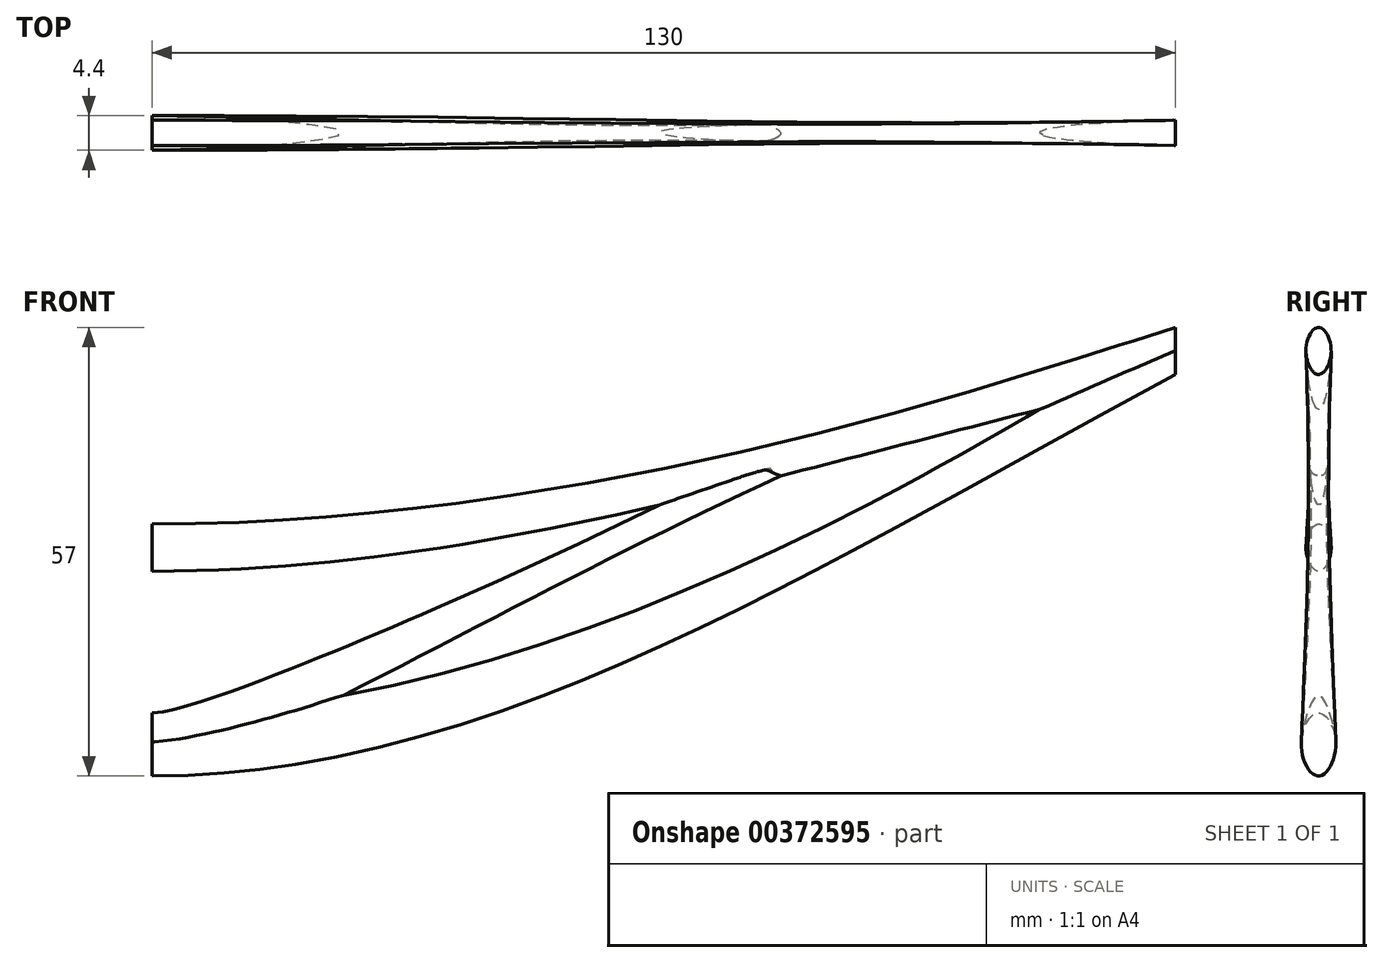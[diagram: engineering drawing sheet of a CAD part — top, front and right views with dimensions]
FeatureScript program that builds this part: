
annotation { "Feature Type Name" : "Feature", "Feature Type Description" : "" }
export const myFeature = defineFeature(function(context is Context, id is Id, definition is map)
    precondition{}
    {
        {
            var Q0;
            Q0=qCreatedBy(makeId("Right.planeOp"),FACE);
            var sketch = newSketch(context, id + "F0", { "sketchPlane" : qUnion([Q0])});
            skFitSpline(sketch, "E0", {"points": [v(-2.2, 0) * mm, v(0, 4) * mm, v(2.2, 0) * mm, v(0, -4) * mm, v(-2.2, 0) * mm]});
            skPoint(sketch, "E1", {"position": v(0, 25) * mm});
            skFitSpline(sketch, "E2", {"points": [v(-1.6, 25) * mm, v(0, 28) * mm, v(1.6, 25) * mm, v(0, 22) * mm, v(-1.6, 25) * mm]});
            skSolve(sketch);
        }
        {
            var Q0;
            Q0=qCreatedBy(makeId("Right.planeOp"),FACE);
            cPlane(context, id + "F1", {"entities" : qUnion([Q0]), "cplaneType" : CPlaneType.OFFSET, "offset" : 130 * mm, "width" : 150 * mm, "height" : 150 * mm});
        }
        {
            var Q0;
            Q0=qCreatedBy(id+"F1.planeOp",FACE);
            var sketch = newSketch(context, id + "F2", { "sketchPlane" : qUnion([Q0])});
            skFitSpline(sketch, "E3", {"points": [v(-1.6, 50) * mm, v(0, 53) * mm, v(1.6, 50) * mm, v(0, 47) * mm, v(-1.6, 50) * mm]});
            skFitSpline(sketch, "E4.0", {"points": [v(-3, 0) * mm, v(-3, 2.5) * mm, v(0, 7.5) * mm, v(4.5, 0) * mm, v(0, -7.5) * mm, v(-3, -2.5) * mm, v(-3, 0) * mm]});
            skPoint(sketch, "E5.0", {"position": v(0, 0) * mm});
            skLineSegment(sketch, "E6", {"start": v(-1.6, 50) * mm, "end": v(0, 50) * mm, "construction": true});
            skLineSegment(sketch, "E7", {"start": v(0, 50) * mm, "end": v(1.6, 50) * mm, "construction": true});
            skLineSegment(sketch, "E8", {"start": v(0, 50) * mm, "end": v(0, 53) * mm, "construction": true});
            skSolve(sketch);
        }
        {
            var Q0;
            Q0=makeQuery(id+"F0.imprint","IMPRINT",FACE,{"disambiguationData":[TD([[makeQuery(id+"F0.imprint","IMPRINT",EDGE,{"derivedFrom":sQuery(id+"F0.wireOp",EDGE,"E0")}),-1.0]])]});
            var Q1;
            Q1=makeQuery(id+"F2.imprint","IMPRINT",FACE,{"disambiguationData":[TD([[makeQuery(id+"F2.imprint","IMPRINT",EDGE,{"derivedFrom":sQuery(id+"F2.wireOp",EDGE,"E3")}),-1.0]])]});
            loft(context, id + "F3", {"startCondition" : LoftEndDerivativeType.NORMAL_TO_PROFILE, "startMagnitude" : 1, "sheetProfilesArray" : [{ "sheetProfileEntities" : qUnion([Q0]) }, { "sheetProfileEntities" : qUnion([Q1]) }]});
        }
        {
            var Q1;
            Q1=makeQuery(id+"F0.imprint","IMPRINT",FACE,{"disambiguationData":[TD([[makeQuery(id+"F0.imprint","IMPRINT",EDGE,{"derivedFrom":sQuery(id+"F0.wireOp",EDGE,"E2")}),-1.0]])]});
            var Q2;
            Q2=makeQuery(id+"F2.imprint","IMPRINT",FACE,{"disambiguationData":[TD([[makeQuery(id+"F2.imprint","IMPRINT",EDGE,{"derivedFrom":sQuery(id+"F2.wireOp",EDGE,"E3")}),-1.0]])]});
            loft(context, id + "F4", {"operationType" : NewBodyOperationType.ADD, "startCondition" : LoftEndDerivativeType.NORMAL_TO_PROFILE, "startMagnitude" : 1, "sheetProfilesArray" : [{ "sheetProfileEntities" : qUnion([Q1]) }, { "sheetProfileEntities" : qUnion([Q2]) }]});
        }
        {
            var Q0;
            Q0=qCreatedBy(makeId("Right.planeOp"),FACE);
            cPlane(context, id + "F5", {"entities" : qUnion([Q0]), "cplaneType" : CPlaneType.OFFSET, "offset" : 80 * mm, "width" : 150 * mm, "height" : 150 * mm});
        }
        {
            var Q0;
            Q0=qCreatedBy(id+"F5.planeOp",FACE);
            var sketch = newSketch(context, id + "F6", { "sketchPlane" : qUnion([Q0])});
            skFitSpline(sketch, "E9", {"points": [v(-1.1, 36.3) * mm, v(0, 38.35) * mm, v(1.1, 36.3) * mm, v(0, 34.2) * mm, v(-1.1, 36.3) * mm]});
            skPoint(sketch, "E10.0", {"position": v(0, 25) * mm});
            skSolve(sketch);
        }
        {
            var Q1;
            Q1=makeQuery(id+"F0.imprint","IMPRINT",FACE,{"disambiguationData":[TD([[makeQuery(id+"F0.imprint","IMPRINT",EDGE,{"derivedFrom":sQuery(id+"F0.wireOp",EDGE,"E0")}),-1.0]])]});
            var Q2;
            Q2 = qSketchRegion(id + "F6", true);
            loft(context, id + "F7", {"operationType" : NewBodyOperationType.ADD, "startCondition" : LoftEndDerivativeType.NORMAL_TO_PROFILE, "startMagnitude" : 0.25, "sheetProfilesArray" : [{ "sheetProfileEntities" : qUnion([Q1]) }, { "sheetProfileEntities" : qUnion([Q2]) }]});
        }
    });
